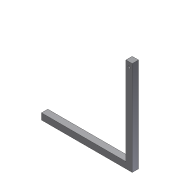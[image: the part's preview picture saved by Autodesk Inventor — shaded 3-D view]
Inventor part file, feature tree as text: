
AUTODESK INVENTOR PART (.ipt)
format: ipt  version: 2012 (Build 160160000, 160)  size: 83,456 bytes
history: native  units: in
note: dims shown in document units (in); Inventor stores cm internally (conversion verified against a paired STEP export)
features: extrude x2, sketch x2
ambient origin geometry x8: Origin, YZ Plane, XZ Plane, XY Plane, X Axis, Y Axis, Z Axis, Center Point
bodies: Solid1 (feature_tree)
feature tree (4):
  extrude  "Extrusion1"  Depth=0.5in
  extrude  "Extrusion2"  Depth=18.0in
  sketch  "Sketch1"  dims[d0=0.375in d2=0.5in]
  sketch  "Sketch2"  dims[d3=1.5in d4=18.0in d5=1.0in d6=0.0in d7=0.5in d8=0.5in d9=0.25in d10=1.0in d11=0.0in]
